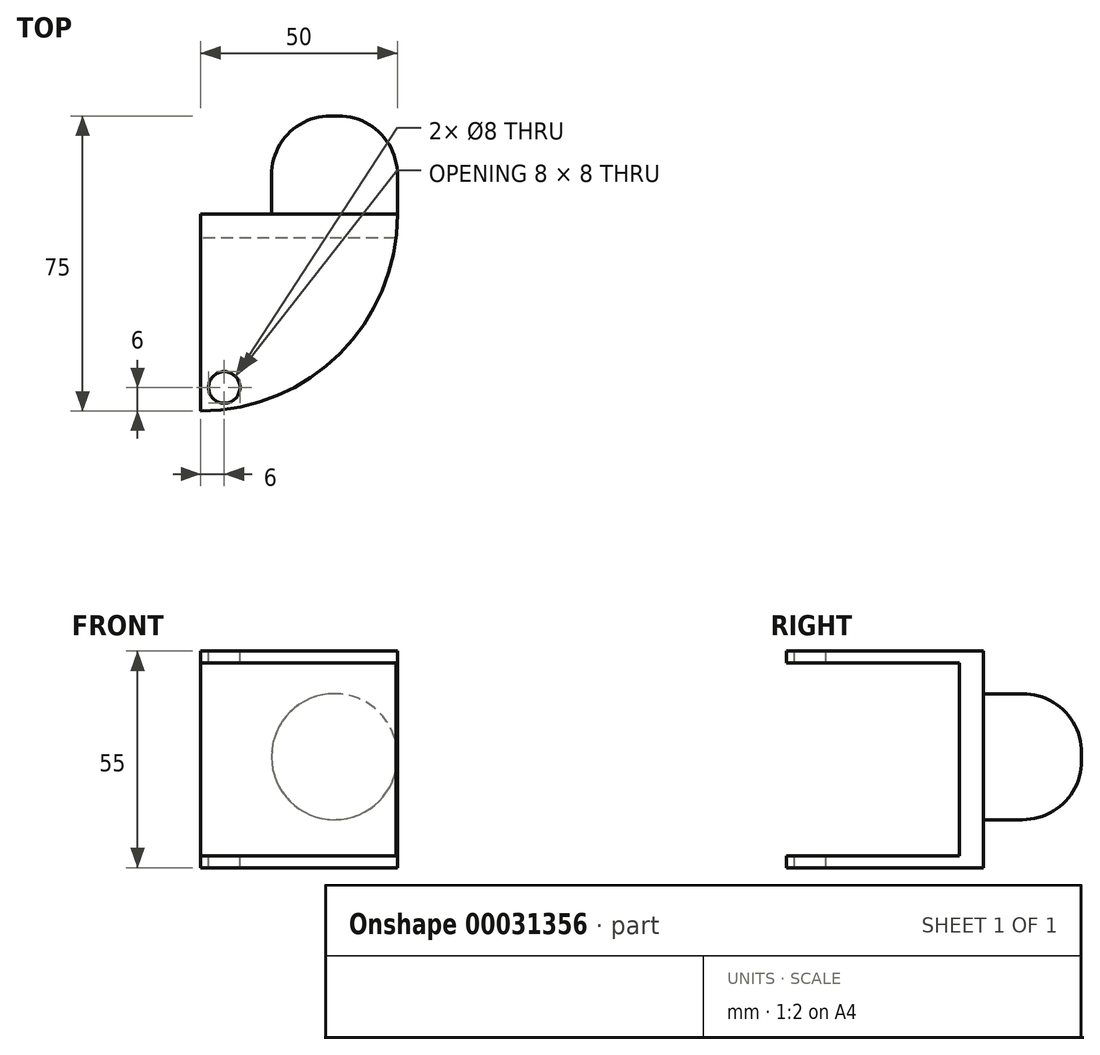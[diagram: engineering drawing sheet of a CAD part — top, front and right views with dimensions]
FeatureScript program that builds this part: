
annotation { "Feature Type Name" : "Feature", "Feature Type Description" : "" }
export const myFeature = defineFeature(function(context is Context, id is Id, definition is map)
    precondition{}
    {
        {
            var Q0;
            Q0=qCreatedBy(makeId("Top.planeOp"),FACE);
            var sketch = newSketch(context, id + "F0", { "sketchPlane" : qUnion([Q0])});
            skArc(sketch, "E0", {"start": v(0, -50) * mm, "mid": v(35.36, -35.36) * mm, "end": v(50, 0) * mm});
            skLineSegment(sketch, "E1", {"start": v(0, 0) * mm, "end": v(0, -50) * mm});
            skLineSegment(sketch, "E2", {"start": v(0, 0) * mm, "end": v(50, 0) * mm});
            skSolve(sketch);
        }
        {
            var Q0;
            Q0 = qSketchRegion(id + "F0", true);
            extrude(context, id + "F1", {"entities" : qUnion([Q0]), "depth" : 55 * mm});
        }
        {
            var Q0;
            Q0=makeQuery(id+"F1.opExtrude","SWEPT_FACE",FACE,{"disambiguationData":[OSD([sQuery(id+"F0.wireOp",EDGE,"E1")])]});
            var sketch = newSketch(context, id + "F2", { "sketchPlane" : qUnion([Q0])});
            skLineSegment(sketch, "E3.bottom", {"start": v(6, 3) * mm, "end": v(50, 3) * mm});
            skLineSegment(sketch, "E3.top", {"start": v(6, 52) * mm, "end": v(50, 52) * mm});
            skLineSegment(sketch, "E3.left", {"start": v(6, 3) * mm, "end": v(6, 52) * mm});
            skLineSegment(sketch, "E3.right", {"start": v(50, 3) * mm, "end": v(50, 52) * mm});
            skSolve(sketch);
        }
        {
            var Q0;
            Q0 = qSketchRegion(id + "F2", true);
            extrude(context, id + "F3", {"entities" : qUnion([Q0]), "operationType" : NewBodyOperationType.REMOVE, "endBound" : BoundingType.THROUGH_ALL, "oppositeDirection" : true, "depth" : 25 * mm});
        }
        {
            var Q0;
            Q0=makeQuery(id+"F1.opExtrude","CAP_FACE",FACE,{"disambiguationData":[OSD([sQuery(id+"F0.wireOp",EDGE,"E0"),sQuery(id+"F0.wireOp",EDGE,"E1"),sQuery(id+"F0.wireOp",EDGE,"E2")])],"isStart":false});
            var sketch = newSketch(context, id + "F4", { "sketchPlane" : qUnion([Q0])});
            skCircle(sketch, "E4", {"center": v(6, -44) * mm, "radius": 4 * mm});
            skSolve(sketch);
        }
        {
            var Q0;
            Q0 = qSketchRegion(id + "F4", true);
            extrude(context, id + "F5", {"entities" : qUnion([Q0]), "operationType" : NewBodyOperationType.REMOVE, "oppositeDirection" : true, "depth" : 55 * mm});
        }
        {
            var Q0;
            Q0=makeQuery(id+"F1.opExtrude","SWEPT_FACE",FACE,{"disambiguationData":[OSD([sQuery(id+"F0.wireOp",EDGE,"E2")])]});
            var sketch = newSketch(context, id + "F6", { "sketchPlane" : qUnion([Q0])});
            skCircle(sketch, "E5", {"center": v(-34, 28.18) * mm, "radius": 16 * mm});
            skSolve(sketch);
        }
        {
            var Q0;
            Q0 = qSketchRegion(id + "F6", true);
            extrude(context, id + "F7", {"entities" : qUnion([Q0]), "operationType" : NewBodyOperationType.ADD, "depth" : 25 * mm});
        }
        {
            var Q0;
            Q0=makeQuery(id+"F7.opExtrude","CAP_EDGE",EDGE,{"disambiguationData":[OSD([sQuery(id+"F6.wireOp",EDGE,"E5")])],"isStart":false});
            fillet(context, id + "F8", {"entities" : qUnion([Q0]), "radius" : 15 * mm, "tangentPropagation" : true, "allowEdgeOverflow" : false});
        }
    });
